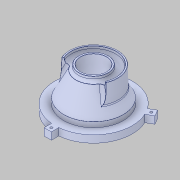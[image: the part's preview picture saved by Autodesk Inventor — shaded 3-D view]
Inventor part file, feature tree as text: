
AUTODESK INVENTOR PART (.ipt)
format: ipt  version: 2019 (Build 230136000, 136)  size: 521,728 bytes
history: native  units: in
note: dims shown in document units (in); Inventor stores cm internally (conversion verified against a paired STEP export)
features: extrude x3, sketch x3, boolean_combine x1, delete_face x1, pattern_circular x1, other x1
ambient origin geometry x8: Origin, YZ Plane, XZ Plane, XY Plane, X Axis, Y Axis, Z Axis, Center Point
bodies: Solid1 (feature_tree), Solid2 (feature_tree)
feature tree (10):
  extrude  "Extrusion1"  Depth=3.1496in TaperAngle=0.0deg
  boolean_combine  "Combine1"
  delete_face  "Delete Face1"
  extrude  "Extrusion5"  Depth=0.5906in TaperAngle=0.0deg
  extrude  "Extrusion7"  Depth=0.5906in
  pattern_circular  "Circular Pattern3"  [2 undecoded]
  sketch  "Sketch1"  dims[d0=5.9055in d1=3.1496in d2=0.0in]
  sketch  "Sketch5"  dims[d17=6.3071in d18=0.5906in d19=0.0in]
  sketch  "Sketch7"  dims[d29=0.5906in d30=1.1811in d31=0.1969in d32=0.2953in d33=0.5906in d34=0.0in d35=1.1811in d36=2.4737in]
  other  "Scale1"
note: 2 required parameter values undecoded (feature->parameter linkage not recoverable at this tier; creation-order binding heuristic only, values carry confidence <= 0.55)
